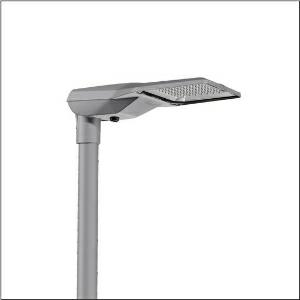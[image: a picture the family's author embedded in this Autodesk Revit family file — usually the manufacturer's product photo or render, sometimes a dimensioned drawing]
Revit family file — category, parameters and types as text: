
# Revit family: streetlight_sl_21_iq_midi___st1_0ab_5xe3m31u08mb_758c
name_source: partatom
category: Lighting Fixtures
units: mm (PartAtom-declared; Revit-internal decimal feet)

## family parameters
Cut with Voids When Loaded = No
Host = Face
Light Source = No
Part Type = Normal
Room Calculation Point = No
Round Connector Dimension = Use Diameter
Shared = No

## types (1)
- --- (1 x LED, 16140 lm, 129.3 W, 3000K)
    Apparent Load = 129 VA
    CIE Flux Codes = 38 73 97 100 100
    Color Rendering = 70
    Color Temperature = 3000K
    Default Elevation = 1800 mm
    Description = Streetlight SL 21 iQ midi, mast luminaire, primary light control with lens, of PMMA, primary optical cover: cover, of toughened safety glass, transparent, light distribution: ST1.0aB, light emission: direct distribution, primary light characteristic: asymmetric, installation type: post-top, side-entry, LED, High Power LED, rated luminous flux: 16.140lm, luminous efficacy: 125lm/W, light colour: 730, colour temperature: 3000K, control gear: iQ-Street Remote, D4i with power reduction, control: pre-setting: logarithmic dimming characteristic, Street-Remote, Auto-Match, Temp-Guard, Lumen-Switch, Night-Set, Smart-Wire, Light-Fading, Desk-Remote (wireless, voltage-free reading and setting of iQ features in the workshop via application-optimized NFC function/RFID function), optimised constant luminous flux control (CLO 2.0), mains connection: 230..240V, AC, 50/60Hz, start of lifetime: 129W, end of service life: 142W, reduction: 56W, luminaire housing, of diecast aluminium, powder-coated, Siteco® metallic grey (DB 702S), corrosivity category C5 mid according to DIN EN ISO 12944, please order mast flange separately, inclination adjustable: 0°, 5°, 10°, 15°, sealing non-destructively replaceable, multi-level sealing system, length: 644mm, width: 335mm, height: 110mm, mast flange for spigot size: 42mm (side-entry): 5XC10008XM4, 60/48mm (side-entry/post-top): 5XC10108XM2, 76/60mm (side-entry/post-top): 5XC10108XM1, mounting height: 4..8m, Smart Interface below, protection rating (complete): IP66, insulation class (complete): insulation class II (safety insulation), certification: CE, ENEC, ENEC+, VDE, impact resistance: IK10, permissible operating ambient temperature for outdoor applications: -40..+50°C, standard-compliant lighting for roads and squares, packaging unit: 1 piece

Light Distribution: ST1.0aB
    Height = 111 mm
    Lamp = 1 x LED
    Lamp Light Flux = 16140 lm
    Lamp Power = 129.3 W
    Lamp count = 1
    Length = 644 mm
    Luminous efficacy = 125 lm/W
    Manufacturer = Siteco
    ModVariant = No
    Model = 5XE3M31U08MB
    Number of Poles = 1
    OnlyDefault = Yes
    Power Factor = 1
    Product Name = Streetlight SL 21 iQ midi | ST1.0aB
    Product group = mast luminaire | pylon top
    ProductGroupID = 6100
    Protection Class = Protection class II
    Protection Degree = IP 66
    RLX_Detail_Level = 1
    RLX_Emergency_Light_Flux = 0 lm
    RLX_Emergency_Type = 0
    RLX_Emergency_Type_DB = No
    RlxData = <blob elided: 91141 chars, md5=326a8698>
    Socket = socket
    Standby Power = 0 W
    System Light Flux = 16141 lm
    System Power = 129 W
    Type Comments = factory setting: luminous flux: 100 % | dim-lin: 254 | 672 mA
    Type Image = l_1004300.jpg
    URL = http://relux.com
    VarID = @adj_133839
    Voltage = 0 V
    Weight = 0.00 kg
    Width = 336 mm

## geometry (parser evidence)
native form markers: Blend x4, Sweep x13
no freeform markers — native parametric forms only
